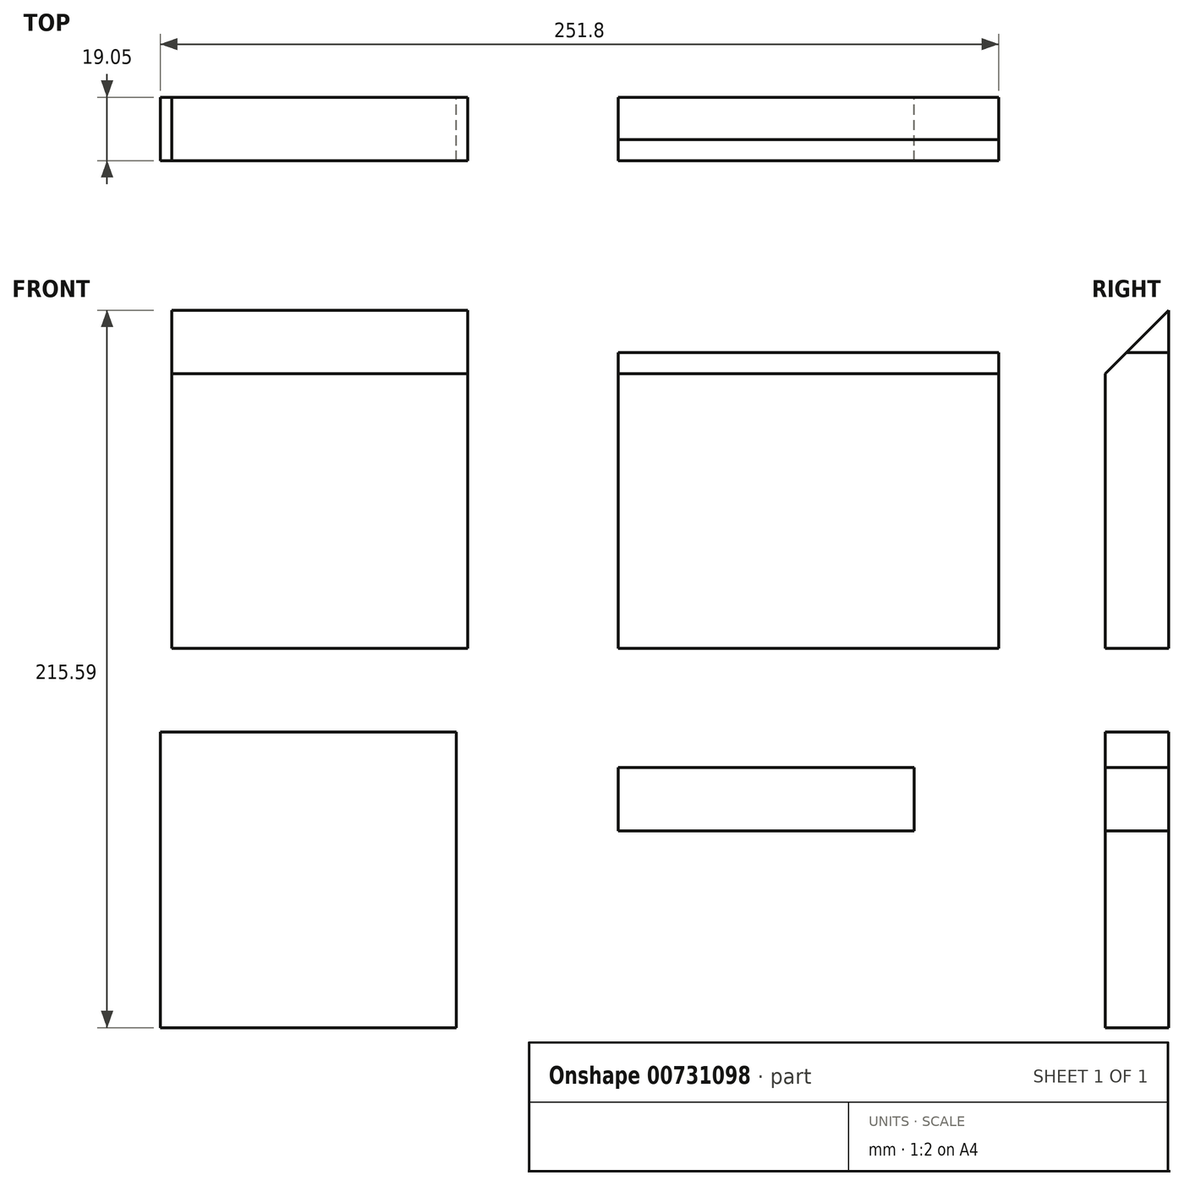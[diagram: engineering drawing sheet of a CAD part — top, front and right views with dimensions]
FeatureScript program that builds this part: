
annotation { "Feature Type Name" : "Feature", "Feature Type Description" : "" }
export const myFeature = defineFeature(function(context is Context, id is Id, definition is map)
    precondition{}
    {
        {
            var Q0;
            Q0=qCreatedBy(makeId("Front.planeOp"),FACE);
            var sketch = newSketch(context, id + "F0", { "sketchPlane" : qUnion([Q0])});
            skLineSegment(sketch, "E0.bottom", {"start": v(0, 0) * mm, "end": v(114.3, 0) * mm});
            skLineSegment(sketch, "E0.top", {"start": v(0, 88.9) * mm, "end": v(114.3, 88.9) * mm});
            skLineSegment(sketch, "E0.left", {"start": v(0, 0) * mm, "end": v(0, 88.9) * mm});
            skLineSegment(sketch, "E0.right", {"start": v(114.3, 0) * mm, "end": v(114.3, 88.9) * mm});
            skSolve(sketch);
        }
        {
            var Q0;
            Q0 = qSketchRegion(id + "F0", true);
            extrude(context, id + "F1", {"entities" : qUnion([Q0]), "depth" : 19.05 * mm, "offsetDistance" : 25.4 * mm});
        }
        {
            var Q0;
            Q0=qCreatedBy(makeId("Front.planeOp"),FACE);
            var sketch = newSketch(context, id + "F2", { "sketchPlane" : qUnion([Q0])});
            skLineSegment(sketch, "E1.bottom", {"start": v(0, -35.79) * mm, "end": v(88.9, -35.79) * mm});
            skLineSegment(sketch, "E1.top", {"start": v(0, -54.84) * mm, "end": v(88.9, -54.84) * mm});
            skLineSegment(sketch, "E1.left", {"start": v(0, -35.79) * mm, "end": v(0, -54.84) * mm});
            skLineSegment(sketch, "E1.right", {"start": v(88.9, -35.79) * mm, "end": v(88.9, -54.84) * mm});
            skSolve(sketch);
        }
        {
            var Q0;
            Q0 = qSketchRegion(id + "F2", true);
            extrude(context, id + "F3", {"entities" : qUnion([Q0]), "depth" : 19.05 * mm, "offsetDistance" : 25.4 * mm});
        }
        {
            var Q0;
            Q0=qCreatedBy(makeId("Front.planeOp"),FACE);
            var sketch = newSketch(context, id + "F4", { "sketchPlane" : qUnion([Q0])});
            skLineSegment(sketch, "E2.bottom", {"start": v(-45.16, 0) * mm, "end": v(-134.06, 0) * mm});
            skLineSegment(sketch, "E2.top", {"start": v(-45.16, 101.6) * mm, "end": v(-134.06, 101.6) * mm});
            skLineSegment(sketch, "E2.left", {"start": v(-45.16, 0) * mm, "end": v(-45.16, 101.6) * mm});
            skLineSegment(sketch, "E2.right", {"start": v(-134.06, 0) * mm, "end": v(-134.06, 101.6) * mm});
            skSolve(sketch);
        }
        {
            var Q0;
            Q0 = qSketchRegion(id + "F4", true);
            extrude(context, id + "F5", {"entities" : qUnion([Q0]), "depth" : 19.05 * mm, "offsetDistance" : 25.4 * mm});
        }
        {
            var Q0;
            Q0=makeQuery(id+"F5.opExtrude","SWEPT_FACE",FACE,{"disambiguationData":[OSD([sQuery(id+"F4.wireOp",EDGE,"E2.right")])]});
            var sketch = newSketch(context, id + "F6", { "sketchPlane" : qUnion([Q0])});
            skLineSegment(sketch, "E3", {"start": v(0, 101.6) * mm, "end": v(19.05, 82.55) * mm});
            skLineSegment(sketch, "E4", {"start": v(19.05, 82.55) * mm, "end": v(19.05, 101.6) * mm});
            skLineSegment(sketch, "E5", {"start": v(19.05, 101.6) * mm, "end": v(0, 101.6) * mm});
            skSolve(sketch);
        }
        {
            var Q0;
            Q0 = qSketchRegion(id + "F6", true);
            extrude(context, id + "F7", {"entities" : qUnion([Q0]), "operationType" : NewBodyOperationType.REMOVE, "endBound" : BoundingType.THROUGH_ALL, "oppositeDirection" : true, "depth" : 25.4 * mm, "offsetDistance" : 25.4 * mm});
        }
        {
            var Q0;
            Q0=qCreatedBy(makeId("Front.planeOp"),FACE);
            var sketch = newSketch(context, id + "F8", { "sketchPlane" : qUnion([Q0])});
            skLineSegment(sketch, "E6.bottom", {"start": v(-137.5, -25.1) * mm, "end": v(-48.6, -25.1) * mm});
            skLineSegment(sketch, "E6.top", {"start": v(-137.5, -114) * mm, "end": v(-48.6, -114) * mm});
            skLineSegment(sketch, "E6.left", {"start": v(-137.5, -25.1) * mm, "end": v(-137.5, -114) * mm});
            skLineSegment(sketch, "E6.right", {"start": v(-48.6, -25.1) * mm, "end": v(-48.6, -114) * mm});
            skSolve(sketch);
        }
        {
            var Q0;
            Q0 = qSketchRegion(id + "F8", true);
            extrude(context, id + "F9", {"entities" : qUnion([Q0]), "depth" : 19.05 * mm, "offsetDistance" : 25.4 * mm});
        }
    });
